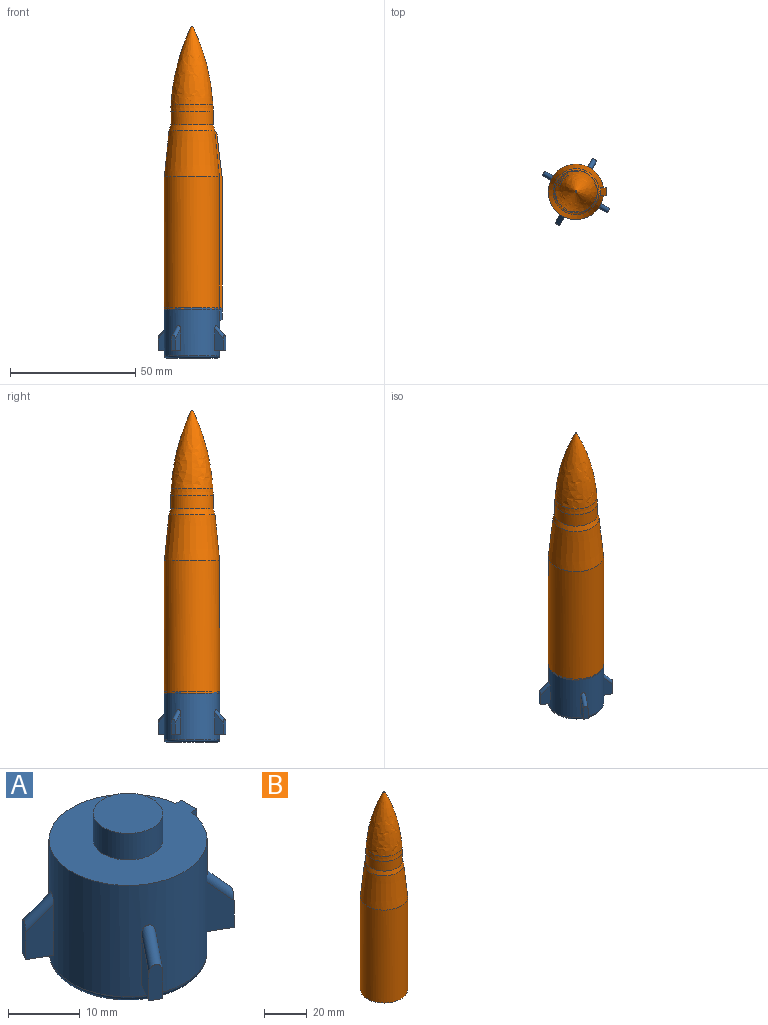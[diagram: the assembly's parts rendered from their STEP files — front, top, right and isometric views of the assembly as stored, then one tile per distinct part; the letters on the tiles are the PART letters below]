
ASSEMBLY  parts=2 mates=1
PART A: 32 faces, bbox 27.6x27.6x24.5 mm
  f0: cylinder r=11mm len=22mm, axis (0,0,-1), area 1220.3mm2, adj f1,f6,f7,f8,f9,f12,f13,f15
  f1: plane 23x22mm, normal (0,0,1), area 309.3mm2, adj f0,f2,f7,f8,f10
  f2: cylinder r=4.85mm len=9.7mm, axis (0,0,-1), area 137.1mm2, adj f1,f3
  f3: plane 9.7x9.7mm, normal (0,0,1), area 73.9mm2, adj f2
  f4: cylinder r=9mm len=18mm, axis (0,0,-1), area 113.1mm2, adj f5,f6
  f5: plane 18x18mm, normal (0,0,-1), area 254.5mm2, adj f4
  f6: torus R=10mm, axis (0,0,1), area 197.4mm2, adj f0,f4
  f7: plane 5x1.1mm, normal (0,-1,0), area 5.4mm2, adj f0,f1,f9,f10,f11
  f8: plane 5x1.1mm, normal (0,1,0), area 5.4mm2, adj f0,f1,f9,f10,f11
  f9: plane 3x0.6mm, normal (0,0,-1), area 1.6mm2, adj f0,f7,f8,f11
  f10: plane 4.5x3mm, normal (1,0,0), area 13.5mm2, adj f1,f7,f8,f11
  f11: plane 3x0.5mm, normal (0.71,0,-0.71), area 2.1mm2, adj f7,f8,f9,f10
  f12: plane 8.63x3.5mm, normal (0.5,0.87,0), area 26.7mm2, adj f0,f14,f15,f29
  f13: plane 8.63x3.5mm, normal (-0.5,-0.87,0), area 26.7mm2, adj f0,f14,f15,f29
  f14: plane 6x1.73mm, normal (-0.87,0.5,0), area 11.4mm2, adj f12,f13,f15,f29
  f15: plane 4.5x3.76mm, normal (0,0,-1), area 8mm2, adj f0,f12,f13,f14
  f16: plane 8.63x3.5mm, normal (0.87,-0.5,0), area 26.7mm2, adj f0,f18,f19,f28
  f17: plane 8.63x3.5mm, normal (-0.87,0.5,0), area 26.7mm2, adj f0,f18,f19,f28
  f18: plane 6x1.73mm, normal (0.5,0.87,0), area 11.4mm2, adj f16,f17,f19,f28
  f19: plane 4.5x3.76mm, normal (0,0,-1), area 8mm2, adj f0,f16,f17,f18
  f20: plane 8.63x3.5mm, normal (-0.5,-0.87,0), area 26.7mm2, adj f0,f22,f23,f30
  f21: plane 8.63x3.5mm, normal (0.5,0.87,0), area 26.7mm2, adj f0,f22,f23,f30
  f22: plane 6x1.73mm, normal (0.87,-0.5,0), area 11.4mm2, adj f20,f21,f23,f30
  f23: plane 4.5x3.76mm, normal (0,0,-1), area 8mm2, adj f0,f20,f21,f22
  f24: plane 8.63x3.5mm, normal (-0.87,0.5,0), area 26.7mm2, adj f0,f26,f27,f31
  f25: plane 8.63x3.5mm, normal (0.87,-0.5,0), area 26.7mm2, adj f0,f26,f27,f31
  f26: plane 6x1.73mm, normal (-0.5,-0.87,0), area 11.4mm2, adj f24,f25,f27,f31
  f27: plane 4.5x3.76mm, normal (0,0,-1), area 8mm2, adj f0,f24,f25,f26
  f28: cylinder r=1mm len=5.41mm, axis (-0.35,-0.61,0.71), area 17.9mm2, adj f0,f16,f17,f18
  f29: cylinder r=1mm len=5.41mm, axis (0.61,-0.35,0.71), area 17.9mm2, adj f0,f12,f13,f14
  f30: cylinder r=1mm len=5.41mm, axis (-0.61,0.35,0.71), area 17.9mm2, adj f0,f20,f21,f22
  f31: cylinder r=1mm len=5.41mm, axis (0.35,0.61,0.71), area 17.9mm2, adj f0,f24,f25,f26
PART B: 19 faces, bbox 23x22x113 mm
  f0: plane 0.15x0.02mm, normal (0,0,1), area 0mm2, adj f4,f10,f18
  f1: cylinder r=11mm len=53mm, axis (0,0,-1), area 3503.6mm2, adj f2,f3,f4,f9,f10
  f2: plane 23x22mm, normal (0,0,-1), area 304.7mm2, adj f1,f9,f10,f12,f13
  f3: cone r=9mm half-angle=5.7deg, axis (0,0,-1), area 2.5mm2, adj f1,f4,f9
  f4: cone r=9mm half-angle=5.7deg, axis (0,0,-1), area 1107.2mm2, adj f0,f1,f3,f8,f10,f11,f18
  f5: cylinder r=8.5mm len=17mm, axis (0,0,-1), area 293.7mm2, adj f7,f8
  f6: plane 0.4x0.4mm, normal (0,0,1), area 0.1mm2, adj f15
  f7: cone r=6.5mm half-angle=3.4deg, axis (0,0,-1), area 144.7mm2, adj f5,f16
  f8: bspline ~18.34x18.34mm, area 129mm2, adj f4,f5
  f9: plane 71.02x2.95mm, normal (0,1,0), area 74.6mm2, adj f1,f2,f3,f11,f12,f17,f18
  f10: plane 71.02x2.95mm, normal (0,-1,0), area 74.6mm2, adj f0,f1,f2,f4,f12,f17,f18
  f11: plane 0.15x0.02mm, normal (0,0,1), area 0mm2, adj f4,f9,f18
  f12: plane 53x3mm, normal (1,0,0), area 159mm2, adj f2,f9,f10,f17
  f13: cylinder r=5mm len=10mm, axis (0,0,-1), area 157.1mm2, adj f2,f14
  f14: plane 10x10mm, normal (0,0,-1), area 78.5mm2, adj f13
  f15: cone r=0.2mm half-angle=25.6deg, axis (0,0,-1), area 0.5mm2, adj f6,f16
  f16: revolved ~31.02x16.68mm, area 1081.1mm2, adj f7,f15
  f17: plane 17.31x3mm, normal (0.99,0,0.12), area 52.3mm2, adj f9,f10,f12,f18
  f18: plane 3x0.79mm, normal (0.66,0,0.75), area 2.9mm2, adj f0,f4,f9,f10,f11,f17
PLACE A t=(-46.96,7.39,-11.46)mm
PLACE B t=(-46.96,7.39,8.04)mm
MATE fastened A.f2 <-> B.f13  axis (0,0,1) through (-46.96,7.39,13.04)mm
